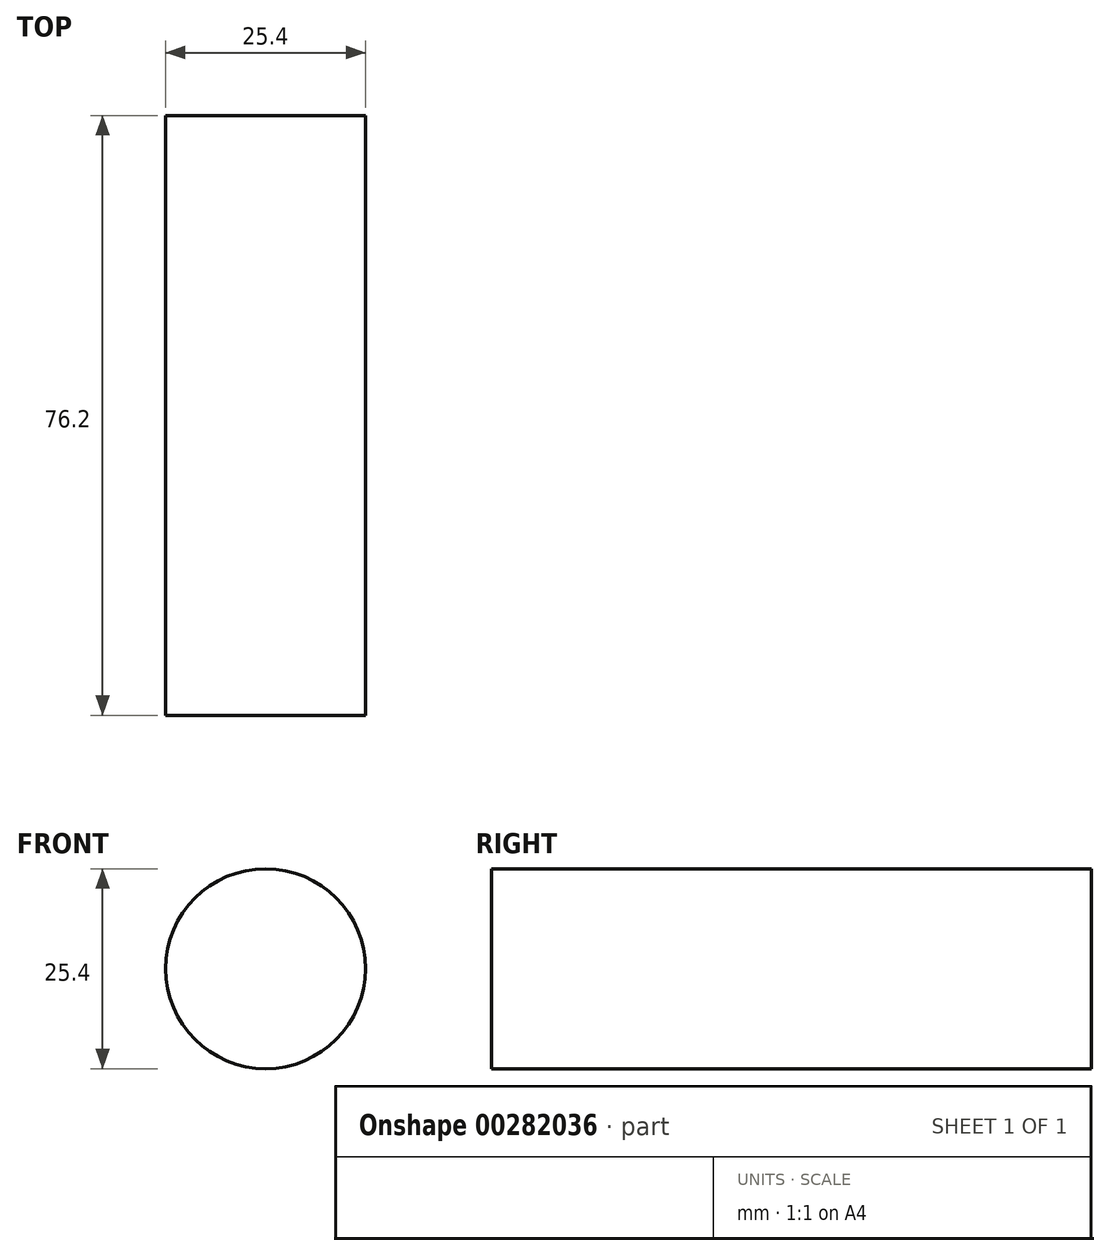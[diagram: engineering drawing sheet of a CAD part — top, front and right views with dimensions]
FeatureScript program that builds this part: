
annotation { "Feature Type Name" : "Feature", "Feature Type Description" : "" }
export const myFeature = defineFeature(function(context is Context, id is Id, definition is map)
    precondition{}
    {
        {
            var Q0;
            Q0=qCreatedBy(makeId("Front.planeOp"),FACE);
            var sketch = newSketch(context, id + "F0", { "sketchPlane" : qUnion([Q0])});
            skCircle(sketch, "E0", {"center": v(-9.17, 23.87) * mm, "radius": 12.7 * mm});
            skSolve(sketch);
        }
        {
            var Q0;
            Q0=makeQuery(id+"F0.imprint","IMPRINT",FACE,{"disambiguationData":[TD([[makeQuery(id+"F0.imprint","IMPRINT",EDGE,{"derivedFrom":sQuery(id+"F0.wireOp",EDGE,"E0")}),1.0]])]});
            extrude(context, id + "F1", {"entities" : qUnion([Q0]), "depth" : 76.2 * mm});
        }
    });
